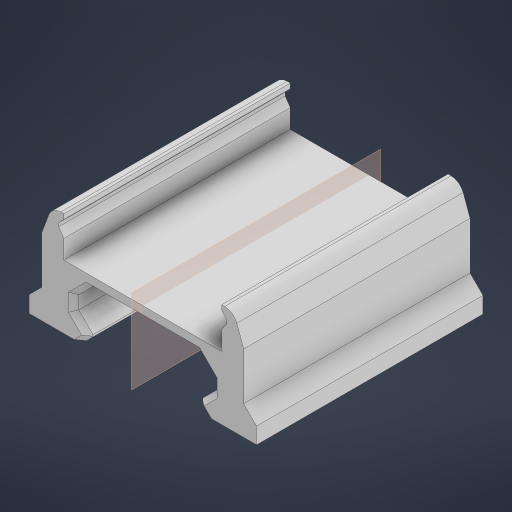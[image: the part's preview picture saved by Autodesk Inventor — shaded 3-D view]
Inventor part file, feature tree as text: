
AUTODESK INVENTOR PART (.ipt)
format: ipt  version: 2023 (Build 270158000, 158)  size: 345,600 bytes
history: native  units: in
note: dims shown in document units (in); Inventor stores cm internally (conversion verified against a paired STEP export)
features: other x4, extrude x3, chamfer x3, projected_geometry x3, sketch x2, reference x2, plane x1, mirror x1, fillet x1
ambient origin geometry x8: Origin, YZ Plane, XZ Plane, XY Plane, X Axis, Y Axis, Z Axis, Center Point
bodies: Solid1 (feature_tree)
feature tree (20):
  extrude  "Extrusion1"  Depth=0.1969in
  plane  "Work Plane2"
  chamfer  "Chamfer1"  Distance=0.1969in
  sketch  "Sketch3"  dims[d0=0.0039in d1=0.1969in]
  chamfer  "Chamfer2"  Distance=1.378in
  extrude  "Extrusion5"  Depth=0.0787in TaperAngle=45.0deg
  mirror  "Mirror3"
  fillet  "Fillet3"  Radius=0.0315in
  extrude  "Extrusion6"  Depth=0.0787in
  chamfer  "Chamfer4"  Distance=0.0787in
  reference  "Reference1"
  reference  "Reference3"
  projected_geometry  "Projected Loop1"
  projected_geometry  "Projected Loop3"
  sketch  "Sketch6"  dims[d2=0.0591in d5=0.1969in d6=1.378in d7=0.0in d8=0.0394in d9=0.125in d10=45.0deg d27=0.0315in d28=0.125in d29=45.0deg d44=0.1575in d45=0.0787in d46=0.0984in d48=0.0157in d49=0.0472in d50=0.481in d51=0.3937in d52=0.0in d53=0.0787in d54=0.0787in d55=0.0in d56=0.0in d57=0.0787in d58=0.0787in d59=45.0deg]
  projected_geometry  "Projected Loop4"
  parser-record x1  (decoder bookkeeping rows leaked as tree rows — omitted from the tree; the rows remain in map.json)
  other  "Rail assembly.iam"
  other  "Picatinny model:1"
  other  "IMU Module:1"
note: 1 file-system path scrubbed to <path> (originals preserved in map.json)
